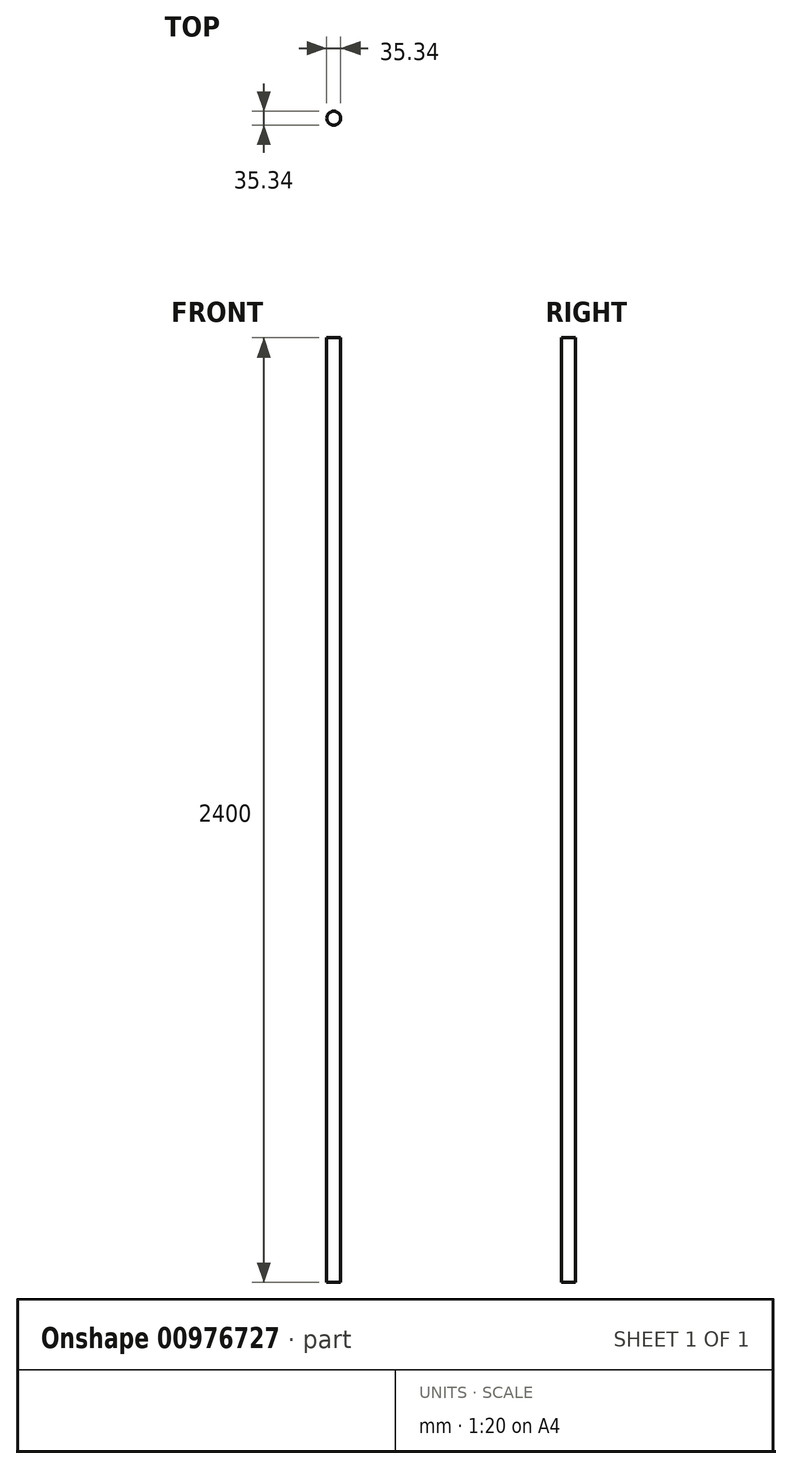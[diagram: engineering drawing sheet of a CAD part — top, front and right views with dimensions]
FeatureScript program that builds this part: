
annotation { "Feature Type Name" : "Feature", "Feature Type Description" : "" }
export const myFeature = defineFeature(function(context is Context, id is Id, definition is map)
    precondition{}
    {
        {
            var Q0;
            Q0=qCreatedBy(makeId("Top.planeOp"),FACE);
            var sketch = newSketch(context, id + "F0", { "sketchPlane" : qUnion([Q0])});
            skCircle(sketch, "E0", {"center": v(0, 0) * mm, "radius": 17.67 * mm});
            skSolve(sketch);
        }
        {
            var Q0;
            Q0=makeQuery(id+"F0.imprint","IMPRINT",FACE,{"disambiguationData":[TD([[makeQuery(id+"F0.imprint","IMPRINT",EDGE,{"derivedFrom":sQuery(id+"F0.wireOp",EDGE,"E0")}),1.0]])]});
            extrude(context, id + "F1", {"entities" : qUnion([Q0]), "depth" : 2400 * mm, "offsetDistance" : 25 * mm});
        }
    });
